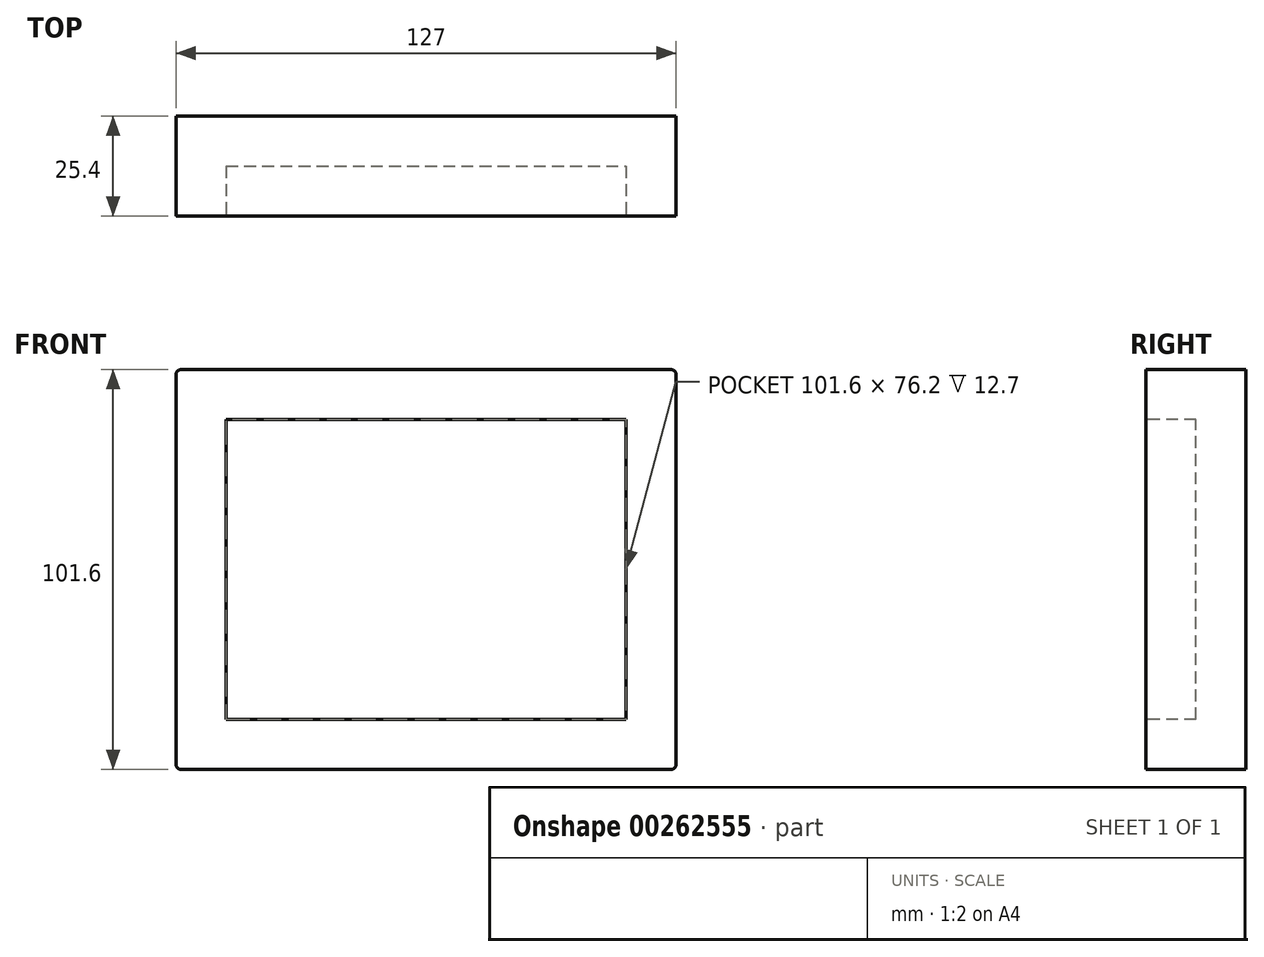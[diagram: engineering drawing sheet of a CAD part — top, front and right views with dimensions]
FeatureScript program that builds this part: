
annotation { "Feature Type Name" : "Feature", "Feature Type Description" : "" }
export const myFeature = defineFeature(function(context is Context, id is Id, definition is map)
    precondition{}
    {
        {
            var Q0;
            Q0=qCreatedBy(makeId("Front.planeOp"),FACE);
            var sketch = newSketch(context, id + "F0", { "sketchPlane" : qUnion([Q0])});
            skLineSegment(sketch, "E0.bottom", {"start": v(-63.5, -50.8) * mm, "end": v(63.5, -50.8) * mm});
            skLineSegment(sketch, "E0.top", {"start": v(-63.5, 50.8) * mm, "end": v(63.5, 50.8) * mm});
            skLineSegment(sketch, "E0.left", {"start": v(-63.5, -50.8) * mm, "end": v(-63.5, 50.8) * mm});
            skLineSegment(sketch, "E0.right", {"start": v(63.5, -50.8) * mm, "end": v(63.5, 50.8) * mm});
            skPoint(sketch, "E0.middle", {"position": v(0, 0) * mm});
            skLineSegment(sketch, "E1.bottom", {"start": v(-50.8, -38.1) * mm, "end": v(50.8, -38.1) * mm});
            skLineSegment(sketch, "E1.top", {"start": v(-50.8, 38.1) * mm, "end": v(50.8, 38.1) * mm});
            skLineSegment(sketch, "E1.left", {"start": v(-50.8, -38.1) * mm, "end": v(-50.8, 38.1) * mm});
            skLineSegment(sketch, "E1.right", {"start": v(50.8, -38.1) * mm, "end": v(50.8, 38.1) * mm});
            skSolve(sketch);
        }
        {
            var Q0;
            Q0=makeQuery(id+"F0.imprint","IMPRINT",FACE,{"disambiguationData":[TD([[makeQuery(id+"F0.imprint","IMPRINT",EDGE,{"derivedFrom":sQuery(id+"F0.wireOp",EDGE,"E0.bottom")}),1.0]])]});
            var Q1;
            Q1=makeQuery(id+"F0.imprint","IMPRINT",FACE,{"disambiguationData":[TD([[makeQuery(id+"F0.imprint","IMPRINT",EDGE,{"derivedFrom":sQuery(id+"F0.wireOp",EDGE,"E1.bottom")}),1.0]])]});
            extrude(context, id + "F1", {"entities" : qUnion([Q0, Q1]), "oppositeDirection" : true, "depth" : 25.4 * mm});
        }
        {
            var Q0;
            Q0=makeQuery(id+"F0.imprint","IMPRINT",FACE,{"disambiguationData":[TD([[makeQuery(id+"F0.imprint","IMPRINT",EDGE,{"derivedFrom":sQuery(id+"F0.wireOp",EDGE,"E1.bottom")}),1.0]])]});
            extrude(context, id + "F2", {"entities" : qUnion([Q0]), "operationType" : NewBodyOperationType.REMOVE, "oppositeDirection" : true, "depth" : 12.7 * mm});
        }
        {
            var Q0;
            Q0=makeQuery(id+"F1.opExtrude","SWEPT_EDGE",EDGE,{"disambiguationData":[OSD([sQuery(id+"F0.wireOp",EDGE,"E0.top"),sQuery(id+"F0.wireOp",EDGE,"E0.left")])]});
            var Q1;
            Q1=makeQuery(id+"F1.opExtrude","SWEPT_EDGE",EDGE,{"disambiguationData":[OSD([sQuery(id+"F0.wireOp",EDGE,"E0.top"),sQuery(id+"F0.wireOp",EDGE,"E0.right")])]});
            var Q2;
            Q2=makeQuery(id+"F1.opExtrude","SWEPT_EDGE",EDGE,{"disambiguationData":[OSD([sQuery(id+"F0.wireOp",EDGE,"E0.bottom"),sQuery(id+"F0.wireOp",EDGE,"E0.right")])]});
            var Q3;
            Q3=makeQuery(id+"F1.opExtrude","SWEPT_EDGE",EDGE,{"disambiguationData":[OSD([sQuery(id+"F0.wireOp",EDGE,"E0.bottom"),sQuery(id+"F0.wireOp",EDGE,"E0.left")])]});
            fillet(context, id + "F3", {"entities" : qUnion([Q0, Q1, Q2, Q3]), "radius" : 1.27 * mm, "tangentPropagation" : true, "allowEdgeOverflow" : false});
        }
    });
